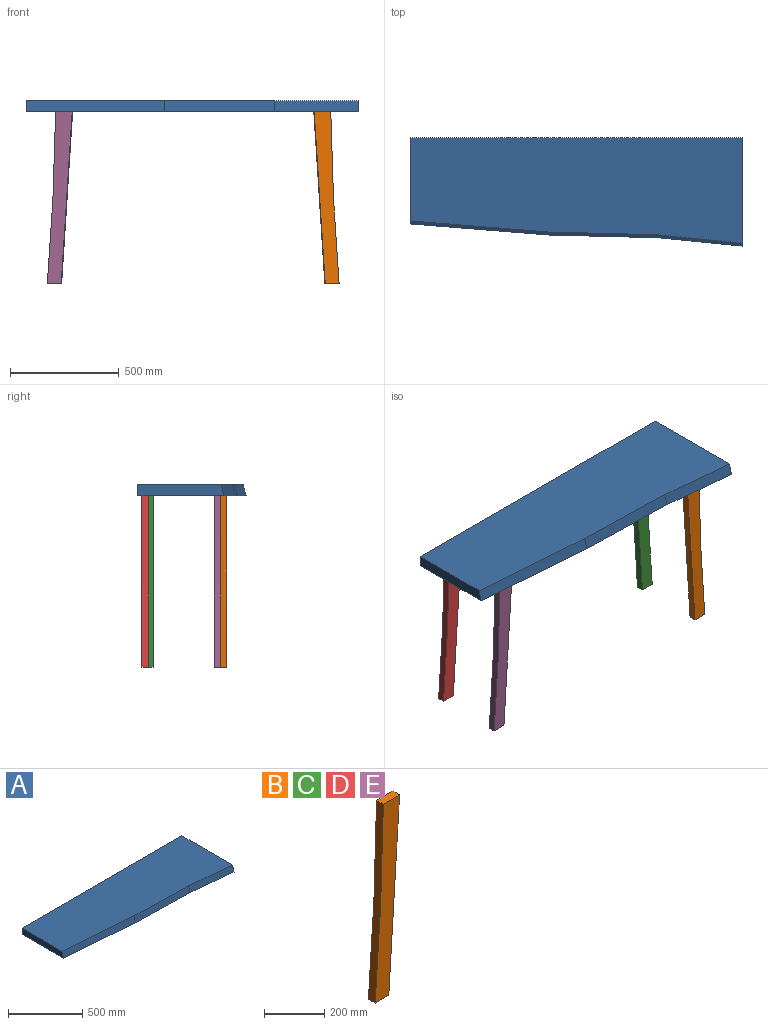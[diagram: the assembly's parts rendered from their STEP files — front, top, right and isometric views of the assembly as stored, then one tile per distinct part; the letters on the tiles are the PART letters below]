
ASSEMBLY  parts=5 mates=4
PART A: 8 faces, bbox 1524x496.3x50.8 mm
  f0: plane 1524x50.8mm, normal (0,1,0), area 77419.2mm2, adj f1,f5,f6,f7
  f1: plane 394.66x50.8mm, normal (-1,0,0), area 19701.6mm2, adj f0,f2,f6,f7
  f2: plane 635x64.4mm, normal (-0.08,-0.96,0.26), area 33483.8mm2, adj f1,f3,f6,f7
  f3: plane 508.71x50.8mm, normal (-0.02,-0.97,0.26), area 26721.5mm2, adj f2,f4,f6,f7
  f4: plane 381.85x51.78mm, normal (-0.1,-0.96,0.26), area 20159.9mm2, adj f3,f5,f6,f7
  f5: plane 496.28x50.8mm, normal (1,0,0), area 24863.5mm2, adj f0,f4,f6,f7
  f6: plane 1524x482.6mm, normal (0,0,1), area 657256.8mm2, adj f0,f1,f2,f3,f4,f5
  f7: plane 1524x496.28mm, normal (0,0,-1), area 678056.8mm2, adj f0,f1,f2,f3,f4,f5
PART B: 6 faces, bbox 114.3x31.8x787.4 mm
  f0: extruded ~787.4x38.1mm, area 25033.4mm2, adj f1,f3,f4,f5
  f1: plane 63.5x31.75mm, normal (0,0,-1), area 2016.1mm2, adj f0,f2,f4,f5
  f2: extruded ~787.4x50.8mm, area 25052mm2, adj f1,f3,f4,f5
  f3: plane 76.2x31.75mm, normal (0,0,1), area 2419.3mm2, adj f0,f2,f4,f5
  f4: plane 787.4x114.3mm, normal (0,-1,0), area 51817.8mm2, adj f0,f1,f2,f3
  f5: plane 787.4x114.3mm, normal (0,1,0), area 51817.8mm2, adj f0,f1,f2,f3
PART C: same geometry as B
PART D: same geometry as B
PART E: same geometry as B
PLACE A t=(306.62,835.3,-70.11)mm fixed
PLACE B rot(axis=(0,0,1),180deg) t=(1781.85,426.51,-70.11)mm
PLACE C rot(axis=(0,0,1),180deg) t=(1779.96,765.84,-70.11)mm
PLACE D t=(368.51,816.92,-70.11)mm
PLACE E t=(366.42,486.14,-70.11)mm
MATE planar A.f7 <-> D.f3  axis (0,0,-1) through (1093.6,612.1,-70.11)mm
MATE planar A.f7 <-> E.f3  axis (0,0,-1) through (1093.6,612.1,-70.11)mm
MATE planar A.f7 <-> B.f3  axis (0,0,-1) through (1093.6,612.1,-70.11)mm
MATE planar A.f7 <-> C.f3  axis (0,0,-1) through (1093.6,612.1,-70.11)mm
